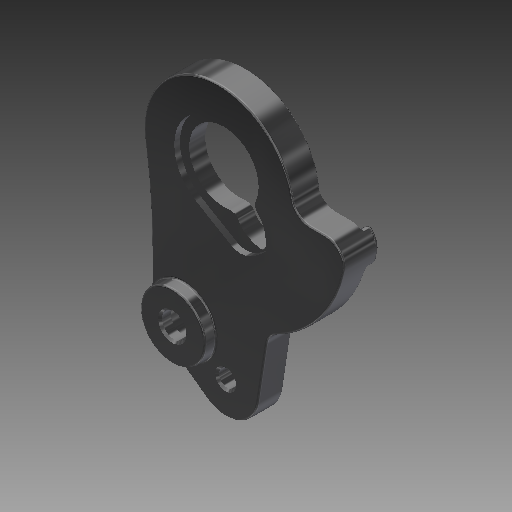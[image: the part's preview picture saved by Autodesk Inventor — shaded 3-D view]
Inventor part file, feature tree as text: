
AUTODESK INVENTOR PART (.ipt)
format: ipt  version: 2019 (Build 230136000, 136)  size: 491,520 bytes
history: native  units: mm
features: fillet x10, sketch x8, extrude x6, hole x2, chamfer x2, plane x2, other x2, mirror x1
ambient origin geometry x8: Origin, YZ Plane, XZ Plane, XY Plane, X Axis, Y Axis, Z Axis, Center Point
bodies: Solid1 (feature_tree)
feature tree (33):
  extrude  "Extrusion1"  Depth=38.460885mm
  extrude  "Extrusion2"  Depth=17.0mm
  fillet  "Fillet1"  Radius=25.961376mm
  extrude  "Extrusion3"  Depth=17.490919mm
  fillet  "Fillet2"  Radius=1.962423mm
  fillet  "Fillet3"  Radius=27.90895mm
  fillet  "Fillet4"  Radius=5.773906mm
  fillet  "Fillet5"  Radius=299.999999mm
  extrude  "Extrusion4"  Depth=10.0mm
  fillet  "Fillet6"  Radius=8.5mm
  hole  "Hole1"  [1 undecoded]
  chamfer  "Chamfer1"  Distance=6.7mm
  hole  "Hole2"  [1 undecoded]
  chamfer  "Chamfer2"  Distance=57.0mm
  fillet  "Fillet7"  Radius=11.840188mm
  fillet  "Fillet8"  Radius=28.484571mm
  fillet  "Fillet9"  Radius=24.371511mm
  fillet  "Fillet10"  Radius=28.5mm
  extrude  "Extrusion5"  Depth=1.5mm
  extrude  "Extrusion6"  Depth=1.5mm
  plane  "Work Plane1"
  mirror  "Mirror1"
  plane  "Work Plane2"
  sketch  "Sketch1"  dims[d0=39.0mm d1=38.460885mm]
  sketch  "Sketch2"  dims[d2=9.000017mm d3=17.0mm d4=25.961376mm]
  sketch  "Sketch3"  dims[d5=167.500017mm d6=17.490919mm d7=1.962423mm d8=27.90895mm d9=5.773906mm d10=299.999999mm]
  sketch  "Sketch4"  dims[d11=17.0mm d12=10.0mm d13=10.0mm d14=8.5mm]
  sketch  "Sketch5"  dims[d15=8.5mm d16=34.297439mm]
  sketch  "Sketch6"  dims[d17=46.458437mm d18=6.7mm d19=0.0mm]
  sketch  "Sketch7"  dims[d20=3.0mm d21=0.0mm d22=0.5mm d23=57.0mm d24=67.0mm d25=11.840188mm d26=28.484571mm d27=24.371511mm d28=28.5mm]
  sketch  "Sketch8"  dims[d29=33.5mm d30=9.599399mm d31=28.159468mm d32=28.461988mm d33=33.495958mm d34=6.704326mm d35=8.805553mm d36=13.835492mm d37=2.7mm d38=0.0mm d39=1.0mm d40=1.0mm d41=1.0mm d42=0.5mm d43=0.5mm d44=0.0mm d45=5.0mm d46=6.45mm d47=6.0mm d48=10.0mm d49=6.9mm d50=90.0deg d51=8.0mm d52=0.0mm d53=0.5mm d54=2.0mm d55=45.0deg d56=4.5mm d57=6.0mm d58=10.0mm d59=6.7mm d60=90.0deg d61=8.0mm d62=20.594885mm d63=0.5mm d64=2.0mm d65=45.0deg d66=0.5mm d67=0.25mm d68=0.5mm d69=0.5mm d70=19.0mm d71=9.668574mm d72=12.560799mm d73=10.966449mm d74=4.41269mm d75=4.580212mm d76=10.439428mm d77=4.6mm d79=10.0mm d80=1.249172mm d81=9.5mm d82=5.0mm d83=2.3mm d84=9.1mm d85=0.5mm d86=0.0mm d87=35.000385mm d88=23.0mm d89=3.839724mm d90=3.839724mm d91=5.0mm d92=1.5mm d93=0.0mm]
  other  "Work Axis1"
  other  "Work Axis2"
note: 2 required parameter values undecoded (feature->parameter linkage not recoverable at this tier; creation-order binding heuristic only, values carry confidence <= 0.55)
